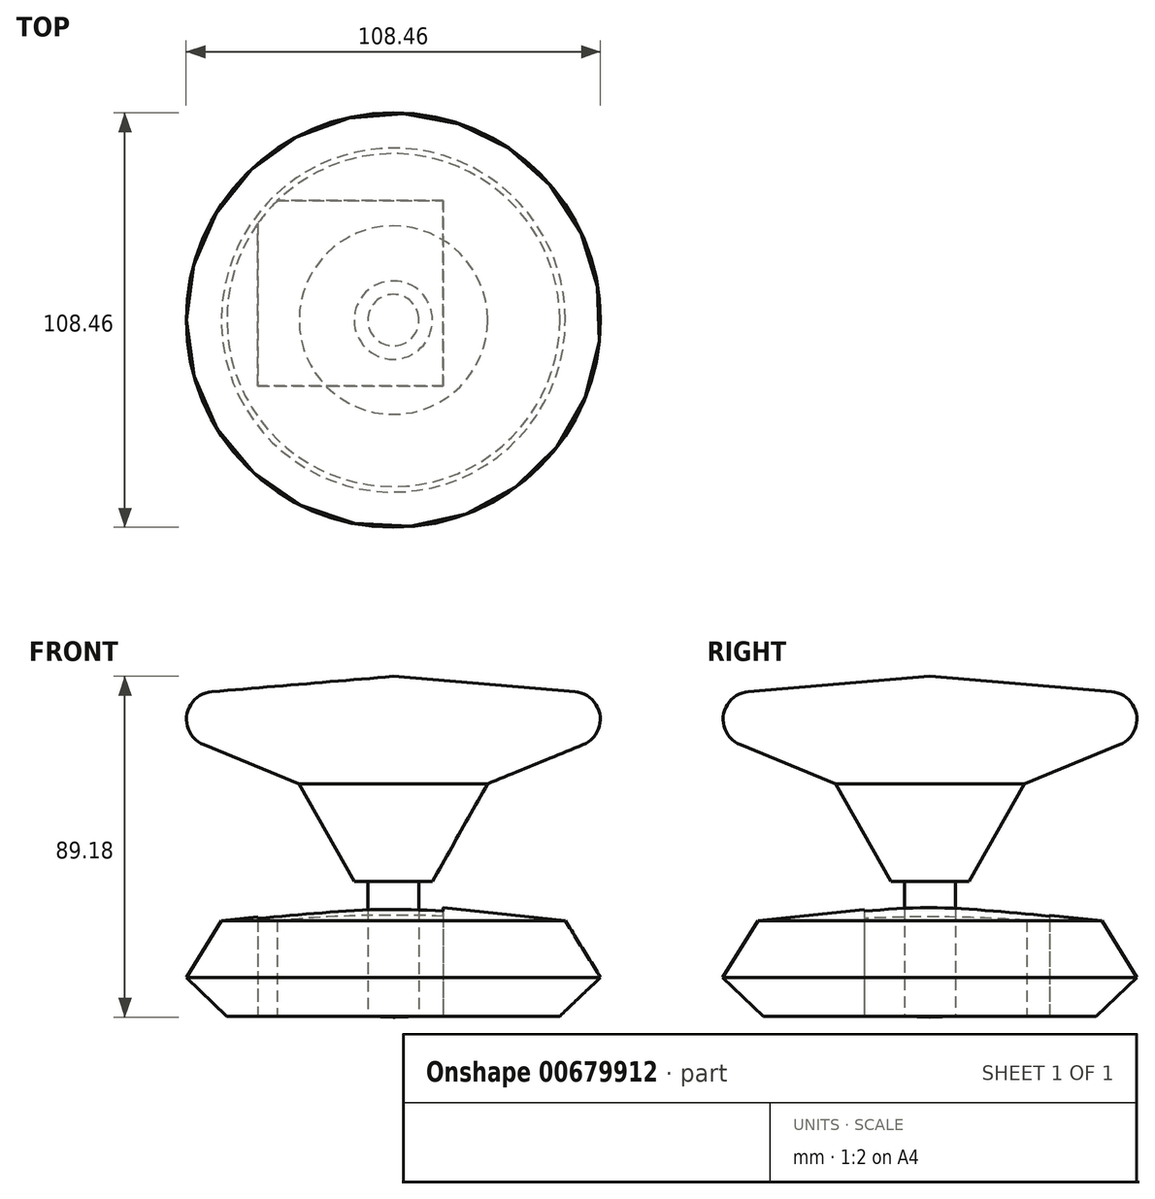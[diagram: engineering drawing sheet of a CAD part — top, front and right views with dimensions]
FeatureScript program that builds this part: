
annotation { "Feature Type Name" : "Feature", "Feature Type Description" : "" }
export const myFeature = defineFeature(function(context is Context, id is Id, definition is map)
    precondition{}
    {
        {
            var Q0;
            Q0=qCreatedBy(makeId("Front.planeOp"),FACE);
            var sketch = newSketch(context, id + "F0", { "sketchPlane" : qUnion([Q0])});
            skLineSegment(sketch, "E0", {"start": v(0, 0) * mm, "end": v(0, 45.68) * mm, "construction": true});
            skLineSegment(sketch, "E1", {"start": v(-6.73, -21.21) * mm, "end": v(-43.56, -21.21) * mm});
            skLineSegment(sketch, "E2", {"start": v(-43.56, -21.21) * mm, "end": v(-54.23, -11.03) * mm});
            skLineSegment(sketch, "E3", {"start": v(-54.23, -11.03) * mm, "end": v(-45.02, 3.75) * mm});
            skLineSegment(sketch, "E4", {"start": v(-45.02, 3.75) * mm, "end": v(-6.73, 7.87) * mm});
            skLineSegment(sketch, "E5", {"start": v(-6.73, 7.87) * mm, "end": v(-24.66, 39.62) * mm});
            skLineSegment(sketch, "E6", {"start": v(-24.66, 39.62) * mm, "end": v(-77.5, 61.19) * mm});
            skLineSegment(sketch, "E7", {"start": v(-77.5, 61.19) * mm, "end": v(0, 67.73) * mm});
            skLineSegment(sketch, "E8", {"start": v(0, 67.73) * mm, "end": v(0, -21.45) * mm});
            skLineSegment(sketch, "E9", {"start": v(0, -21.45) * mm, "end": v(-6.73, -21.21) * mm});
            skSolve(sketch);
        }
        {
            var Q0;
            Q0=makeQuery(id+"F0.imprint","IMPRINT",FACE,{"disambiguationData":[TD([[makeQuery(id+"F0.imprint","IMPRINT",EDGE,{"derivedFrom":sQuery(id+"F0.wireOp",EDGE,"E1")}),-1.0]])]});
            var Q1;
            Q1=sQuery(id+"F0.wireOp",EDGE,"E8");
            revolve(context, id + "F1", {"entities" : qUnion([Q0]), "axis" : qUnion([Q1]), "revolveType" : RevolveType.FULL});
        }
        {
            var Q0;
            Q0=makeQuery(id+"F1.opRevolve","SWEPT_EDGE",EDGE,{"disambiguationData":[OSD([sQuery(id+"F0.wireOp",EDGE,"E6"),sQuery(id+"F0.wireOp",EDGE,"E7")])]});
            fillet(context, id + "F2", {"entities" : qUnion([Q0]), "radius" : 7.23 * mm, "tangentPropagation" : true, "allowEdgeOverflow" : false});
        }
        {
            var Q0;
            Q0=makeQuery(id+"F1.opRevolve","SWEPT_FACE",FACE,{"disambiguationData":[OSD([sQuery(id+"F0.wireOp",EDGE,"E1")])]});
            var sketch = newSketch(context, id + "F3", { "sketchPlane" : qUnion([Q0])});
            skLineSegment(sketch, "E10.bottom", {"start": v(13.05, -31.25) * mm, "end": v(-35.47, -31.25) * mm});
            skLineSegment(sketch, "E10.top", {"start": v(13.05, 17.17) * mm, "end": v(-35.47, 17.17) * mm});
            skLineSegment(sketch, "E10.left", {"start": v(13.05, -31.25) * mm, "end": v(13.05, 17.17) * mm});
            skLineSegment(sketch, "E10.right", {"start": v(-35.47, -31.25) * mm, "end": v(-35.47, 17.17) * mm});
            skSolve(sketch);
        }
        {
            var Q0;
            {var subQ1=sQuery(id+"F3.wireOp",EDGE,"E10.top");Q0=makeQuery(id+"F3.imprint","IMPRINT",FACE,{"disambiguationData":[TD([[makeQuery(id+"F3.imprint","IMPRINT",EDGE,{"derivedFrom":subQ1}),1.0]])]});}
            var Q1;
            Q1=sQuery(id+"F3.wireOp",EDGE,"E10.left");
            extrude(context, id + "F4", {"entities" : qUnion([Q0]), "operationType" : NewBodyOperationType.REMOVE, "surfaceEntities" : qUnion([Q1]), "endBound" : BoundingType.SYMMETRIC, "oppositeDirection" : true, "depth" : 70.6 * mm, "offsetDistance" : 25 * mm});
        }
    });
